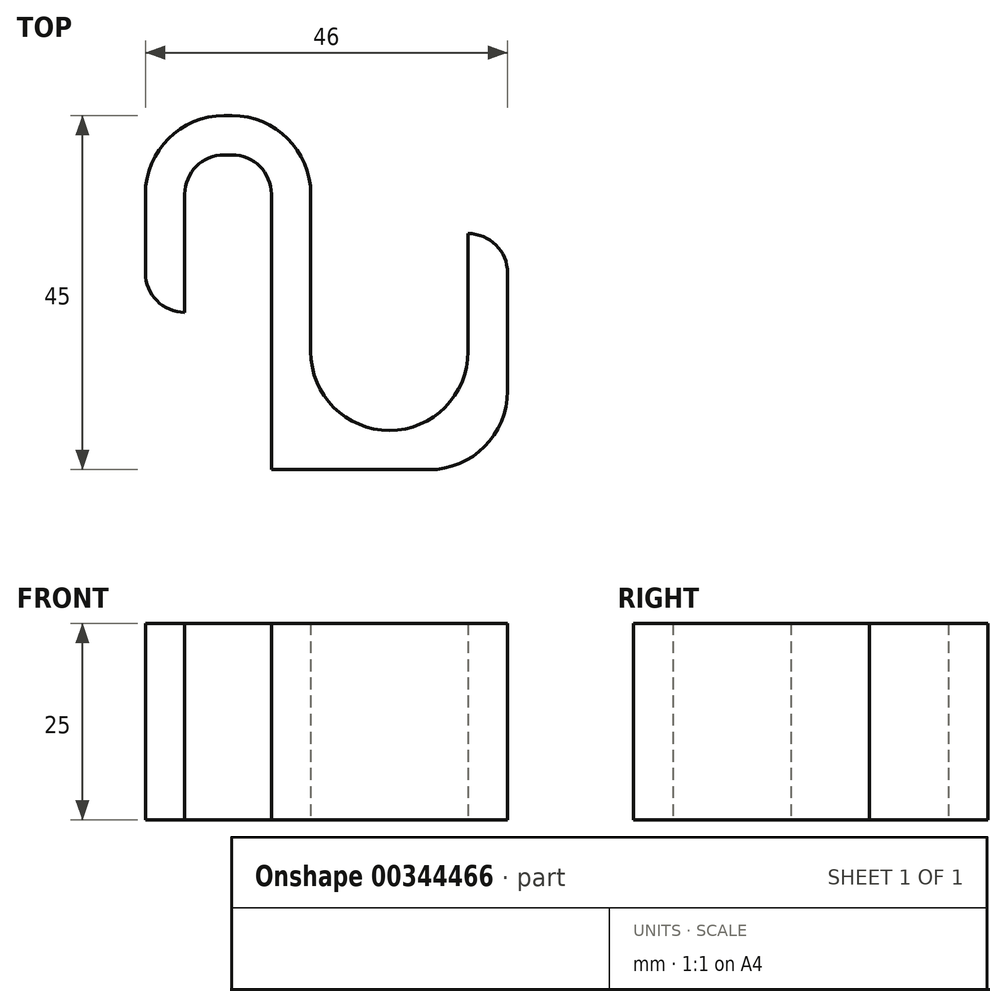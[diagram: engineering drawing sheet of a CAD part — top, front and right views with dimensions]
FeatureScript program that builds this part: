
annotation { "Feature Type Name" : "Feature", "Feature Type Description" : "" }
export const myFeature = defineFeature(function(context is Context, id is Id, definition is map)
    precondition{}
    {
        {
            var Q0;
            Q0=qCreatedBy(makeId("Top.planeOp"),FACE);
            var sketch = newSketch(context, id + "F0", { "sketchPlane" : qUnion([Q0])});
            skLineSegment(sketch, "E0", {"start": v(-11, 0) * mm, "end": v(-11, 15) * mm});
            skLineSegment(sketch, "E1", {"start": v(-6, 20) * mm, "end": v(-5, 20) * mm});
            skLineSegment(sketch, "E2", {"start": v(0, 15) * mm, "end": v(0, -20) * mm});
            skLineSegment(sketch, "E3", {"start": v(0, -20) * mm, "end": v(20, -20) * mm});
            skLineSegment(sketch, "E4", {"start": v(30, -10) * mm, "end": v(30, 10) * mm});
            skLineSegment(sketch, "E5.0", {"start": v(25, -5) * mm, "end": v(25, -1.1) * mm});
            skLineSegment(sketch, "E5.1", {"start": v(-16, 0) * mm, "end": v(-16, 15) * mm});
            skLineSegment(sketch, "E5.2", {"start": v(-6, 25) * mm, "end": v(-5, 25) * mm});
            skLineSegment(sketch, "E5.3", {"start": v(5, 15) * mm, "end": v(5, -5) * mm});
            skLineSegment(sketch, "E5.4", {"start": v(15, -15) * mm, "end": v(15, -15) * mm});
            skLineSegment(sketch, "E6", {"start": v(-16, 0) * mm, "end": v(-11, 0) * mm});
            skLineSegment(sketch, "E7", {"start": v(25, -1.1) * mm, "end": v(25, 10) * mm});
            skLineSegment(sketch, "E8", {"start": v(25, 10) * mm, "end": v(30, 10) * mm});
            skPoint(sketch, "E9.visualSharp", {"position": v(-11, 20) * mm});
            skArc(sketch, "E9.filletArc", {"start": v(-6, 20) * mm, "mid": v(-9.54, 18.54) * mm, "end": v(-11, 15) * mm});
            skPoint(sketch, "E10.visualSharp", {"position": v(0, 20) * mm});
            skArc(sketch, "E10.filletArc", {"start": v(0, 15) * mm, "mid": v(-1.46, 18.54) * mm, "end": v(-5, 20) * mm});
            skPoint(sketch, "E11.visualSharp", {"position": v(5, -15) * mm});
            skArc(sketch, "E11.filletArc", {"start": v(5, -5) * mm, "mid": v(7.93, -12.07) * mm, "end": v(15, -15) * mm});
            skPoint(sketch, "E12.visualSharp", {"position": v(25, -15) * mm});
            skArc(sketch, "E12.filletArc", {"start": v(15, -15) * mm, "mid": v(22.07, -12.07) * mm, "end": v(25, -5) * mm});
            skPoint(sketch, "E13.visualSharp", {"position": v(-16, 25) * mm});
            skArc(sketch, "E13.filletArc", {"start": v(-6, 25) * mm, "mid": v(-13.07, 22.07) * mm, "end": v(-16, 15) * mm});
            skPoint(sketch, "E14.visualSharp", {"position": v(5, 25) * mm});
            skArc(sketch, "E14.filletArc", {"start": v(5, 15) * mm, "mid": v(2.07, 22.07) * mm, "end": v(-5, 25) * mm});
            skPoint(sketch, "E15.visualSharp", {"position": v(30, -20) * mm});
            skArc(sketch, "E15.filletArc", {"start": v(20, -20) * mm, "mid": v(27.07, -17.07) * mm, "end": v(30, -10) * mm});
            skSolve(sketch);
        }
        {
            var Q0;
            Q0=makeQuery(id+"F0.imprint","IMPRINT",FACE,{"disambiguationData":[TD([[makeQuery(id+"F0.imprint","IMPRINT",EDGE,{"derivedFrom":sQuery(id+"F0.wireOp",EDGE,"E0")}),1.0]])]});
            extrude(context, id + "F1", {"entities" : qUnion([Q0]), "depth" : 25 * mm});
        }
        {
            var Q0;
            Q0=makeQuery(id+"F1.opExtrude","SWEPT_EDGE",EDGE,{"disambiguationData":[OSD([sQuery(id+"F0.wireOp",EDGE,"E4"),sQuery(id+"F0.wireOp",EDGE,"E8")])]});
            fillet(context, id + "F2", {"entities" : qUnion([Q0]), "radius" : 5 * mm, "tangentPropagation" : true, "allowEdgeOverflow" : false});
        }
        {
            var Q0;
            Q0=makeQuery(id+"F1.opExtrude","SWEPT_EDGE",EDGE,{"disambiguationData":[OSD([sQuery(id+"F0.wireOp",EDGE,"E5.1"),sQuery(id+"F0.wireOp",EDGE,"E6")])]});
            fillet(context, id + "F3", {"entities" : qUnion([Q0]), "radius" : 5 * mm, "tangentPropagation" : true, "allowEdgeOverflow" : false});
        }
    });
